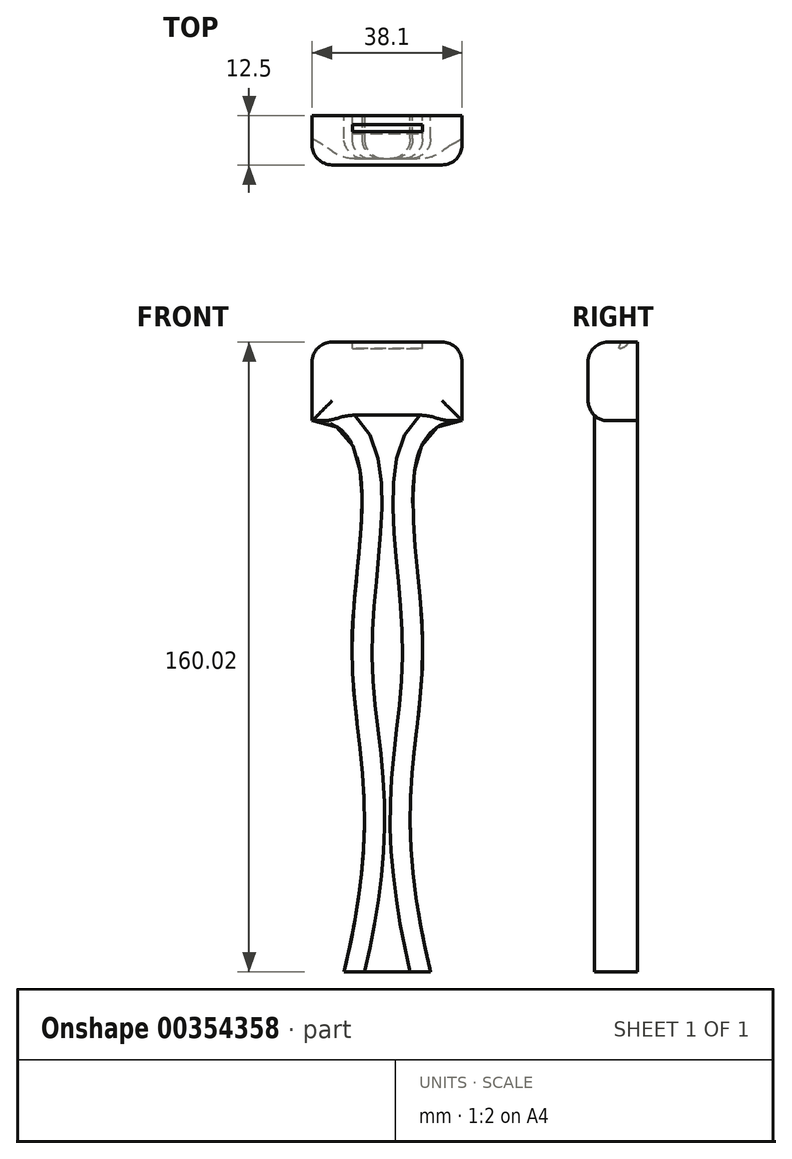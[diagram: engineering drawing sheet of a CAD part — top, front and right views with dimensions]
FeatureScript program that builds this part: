
annotation { "Feature Type Name" : "Feature", "Feature Type Description" : "" }
export const myFeature = defineFeature(function(context is Context, id is Id, definition is map)
    precondition{}
    {
        {
            var Q0;
            Q0=qCreatedBy(makeId("Front.planeOp"),FACE);
            var sketch = newSketch(context, id + "F0", { "sketchPlane" : qUnion([Q0])});
            skPoint(sketch, "E0.middle", {"position": v(0, 0) * mm});
            skFitSpline(sketch, "E1", {"points": [v(-19.1, 53.54) * mm, v(-8.9, 0) * mm, v(-11, -86.48) * mm], "startDerivative": vector(129.5, 0) * mm, "endDerivative": vector(-59.24, -246.69) * mm});
            skFitSpline(sketch, "E2", {"points": [v(19, 53.54) * mm, v(8.88, 0) * mm, v(11, -86.48) * mm], "startDerivative": vector(-128.81, 0) * mm, "endDerivative": vector(59.24, -246.67) * mm});
            skLineSegment(sketch, "E3", {"start": v(-11, -86.48) * mm, "end": v(11, -86.48) * mm});
            skLineSegment(sketch, "E4", {"start": v(-19.1, 53.54) * mm, "end": v(19, 53.54) * mm});
            skLineSegment(sketch, "E5", {"start": v(0, -86.48) * mm, "end": v(11, -86.48) * mm});
            skLineSegment(sketch, "E6", {"start": v(0, -86.48) * mm, "end": v(-11, -86.48) * mm});
            skLineSegment(sketch, "E7", {"start": v(19, 53.54) * mm, "end": v(19, 73.54) * mm});
            skLineSegment(sketch, "E8", {"start": v(19, 73.54) * mm, "end": v(-19.1, 73.54) * mm});
            skLineSegment(sketch, "E9", {"start": v(-19.1, 73.54) * mm, "end": v(-19.1, 53.54) * mm});
            skLineSegment(sketch, "E10", {"start": v(42.23, 73.54) * mm, "end": v(42.23, -86.48) * mm});
            skSolve(sketch);
        }
        {
            var Q0;
            Q0=makeQuery(id+"F0.imprint","IMPRINT",FACE,{"disambiguationData":[TD([[makeQuery(id+"F0.imprint","IMPRINT",EDGE,{"derivedFrom":sQuery(id+"F0.wireOp",EDGE,"TBdgdQMw-4Niw-TCMF-IJ2J-YXkKBLsSuJYE.bottom")}),1.0]])]});
            var Q1;
            Q1=makeQuery(id+"F0.imprint","IMPRINT",FACE,{"disambiguationData":[TD([[makeQuery(id+"F0.imprint","IMPRINT",EDGE,{"derivedFrom":sQuery(id+"F0.wireOp",EDGE,"E1")}),1.0]])]});
            extrude(context, id + "F1", {"entities" : qUnion([Q0, Q1]), "depth" : 10.92 * mm});
        }
        {
            var Q0;
            Q0=makeQuery(id+"F1.opExtrude","CAP_EDGE",EDGE,{"disambiguationData":[OSD([sQuery(id+"F0.wireOp",EDGE,"E1")])],"isStart":false});
            var Q1;
            Q1=makeQuery(id+"F1.opExtrude","CAP_EDGE",EDGE,{"disambiguationData":[OSD([sQuery(id+"F0.wireOp",EDGE,"E2")])],"isStart":false});
            fillet(context, id + "F2", {"entities" : qUnion([Q0, Q1]), "radius" : 5.08 * mm, "tangentPropagation" : true, "allowEdgeOverflow" : false});
        }
        {
            var Q0;
            Q0=makeQuery(id+"F0.imprint","IMPRINT",FACE,{"disambiguationData":[TD([[makeQuery(id+"F0.imprint","IMPRINT",EDGE,{"derivedFrom":sQuery(id+"F0.wireOp",EDGE,"E4")}),1.0]])]});
            extrude(context, id + "F3", {"entities" : qUnion([Q0]), "operationType" : NewBodyOperationType.ADD, "depth" : 12.5 * mm});
        }
        {
            var Q0;
            Q0=makeQuery(id+"F3.opExtrude","CAP_EDGE",EDGE,{"disambiguationData":[OSD([sQuery(id+"F0.wireOp",EDGE,"E8")])],"isStart":false});
            var Q1;
            Q1=makeQuery(id+"F3.opExtrude","CAP_EDGE",EDGE,{"disambiguationData":[OSD([sQuery(id+"F0.wireOp",EDGE,"E9")])],"isStart":false});
            var Q2;
            Q2=makeQuery(id+"F3.opExtrude","CAP_EDGE",EDGE,{"disambiguationData":[OSD([sQuery(id+"F0.wireOp",EDGE,"E7")])],"isStart":false});
            var Q3;
            Q3=makeQuery(id+"F3.opExtrude","CAP_EDGE",EDGE,{"disambiguationData":[OSD([sQuery(id+"F0.wireOp",EDGE,"E4")])],"isStart":false});
            var Q4;
            Q4=makeQuery(id+"F3.opExtrude","SWEPT_EDGE",EDGE,{"disambiguationData":[OSD([sQuery(id+"F0.wireOp",EDGE,"E8"),sQuery(id+"F0.wireOp",EDGE,"E9")])]});
            var Q5;
            Q5=makeQuery(id+"F3.opExtrude","SWEPT_EDGE",EDGE,{"disambiguationData":[OSD([sQuery(id+"F0.wireOp",EDGE,"E7"),sQuery(id+"F0.wireOp",EDGE,"E8")])]});
            fillet(context, id + "F4", {"entities" : qUnion([Q0, Q1, Q2, Q3, Q4, Q5]), "radius" : 5.08 * mm, "tangentPropagation" : true, "allowEdgeOverflow" : false});
        }
        {
            var Q0;
            Q0=qCreatedBy(makeId("Right.planeOp"),FACE);
            var sketch = newSketch(context, id + "F5", { "sketchPlane" : qUnion([Q0])});
            skFitSpline(sketch, "E11", {"points": [v(-2.25, 73.65) * mm, v(-4.44, 71.87) * mm, v(-4.03, 73.66) * mm], "startDerivative": vector(-1.47, -6.62) * mm, "endDerivative": vector(3.06, 7.74) * mm});
            skLineSegment(sketch, "E12", {"start": v(-4.03, 73.66) * mm, "end": v(-2.25, 73.65) * mm});
            skLineSegment(sketch, "E13", {"start": v(-4.05, 77.56) * mm, "end": v(-2.28, 77.56) * mm});
            skLineSegment(sketch, "E14", {"start": v(-4.03, 71.87) * mm, "end": v(-4.44, 71.87) * mm});
            skFitSpline(sketch, "E15", {"points": [v(-4.05, 77.56) * mm, v(-4, 76.1) * mm, v(-2.28, 77.56) * mm], "startDerivative": vector(-3.03, -7.7) * mm, "endDerivative": vector(1.94, 5.94) * mm});
            skSolve(sketch);
        }
        {
            var Q0;
            Q0 = qSketchRegion(id + "F5", true);
            extrude(context, id + "F6", {"entities" : qUnion([Q0]), "operationType" : NewBodyOperationType.REMOVE, "endBound" : BoundingType.SYMMETRIC, "depth" : 17.78 * mm});
        }
    });
